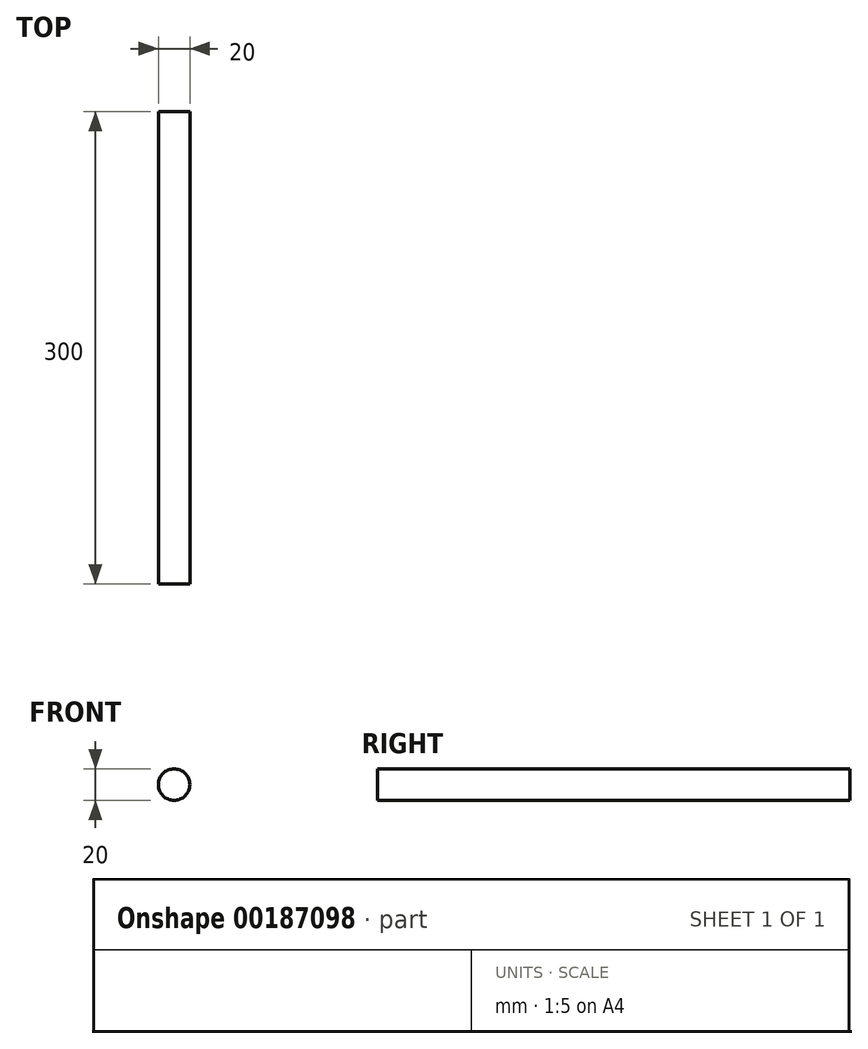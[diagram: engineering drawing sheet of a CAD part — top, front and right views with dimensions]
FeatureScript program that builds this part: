
annotation { "Feature Type Name" : "Feature", "Feature Type Description" : "" }
export const myFeature = defineFeature(function(context is Context, id is Id, definition is map)
    precondition{}
    {
        {
            var Q0;
            Q0=qCreatedBy(makeId("Front.planeOp"),FACE);
            var sketch = newSketch(context, id + "F0", { "sketchPlane" : qUnion([Q0])});
            skCircle(sketch, "E0", {"center": v(0, 0) * mm, "radius": 10 * mm});
            skSolve(sketch);
        }
        {
            var Q0;
            Q0=makeQuery(id+"F0.imprint","IMPRINT",FACE,{"disambiguationData":[TD([[makeQuery(id+"F0.imprint","IMPRINT",EDGE,{"derivedFrom":sQuery(id+"F0.wireOp",EDGE,"E0")}),1.0]])]});
            extrude(context, id + "F1", {"entities" : qUnion([Q0]), "depth" : 300 * mm});
        }
    });
